# Revit family: Keilhauer-Symm-Seater_Bench_RAF_Corner-1
name_source: partatom
category: Furniture
units: mm (PartAtom-declared; Revit-internal decimal feet)

## family parameters
Always vertical = Yes
Cut with Voids When Loaded = No
OmniClass Number = 23.40.20.00
OmniClass Title = General Furniture and Specialties
Room Calculation Point = No
Shared = No
Work Plane-Based = No

## types (6) — shared parameters
Assembly Code = E2020200
Default Elevation = 0"
Depth = 31"
Height = 31"
Keynote = 12500
Low Emitting Finish = Yes
Low Emitting Material = Yes
Manufacturer = Keilhauer
Product Documentation Link = https://keilhauer.com
Revit Model Built By = https://servex-us.com
Salvage or Reuse = Yes
Type Comments = Symm
URL = https://keilhauer.com
WIdth Back = 29 11/16"
Width Seat = 25 3/4"
Width Seat And Back Cushion = 27 5/8"
zero-valued in all types: Percentage of Recycled Content

## per-type parameters (varying)
| type | Back-Seat Cushion | Description | Width |
| 93600 | No | 2-seater RAF corner bench, 4-leg aluminum base | 58 23/32" |
| 93601 | No | 2-seater RAF corner bench, 4-leg ash base | 58 23/32" |
| 93602 | No | 2-seater RAF corner bench, 4-leg walnut base | 58 23/32" |
| 93700 | Yes | 3-seater RAF corner bench, 4-leg aluminum base | 86 11/32" |
| 93701 | Yes | 3-seater RAF corner bench, 4-leg ash base | 86 11/32" |
| 93702 | Yes | 3-seater RAF corner bench, 4-leg walnut base | 86 11/32" |

note: column(s) folded — value = type name in every type: Model

## geometry (parser evidence)
native form markers: Sweep x13
no freeform markers — native parametric forms only
